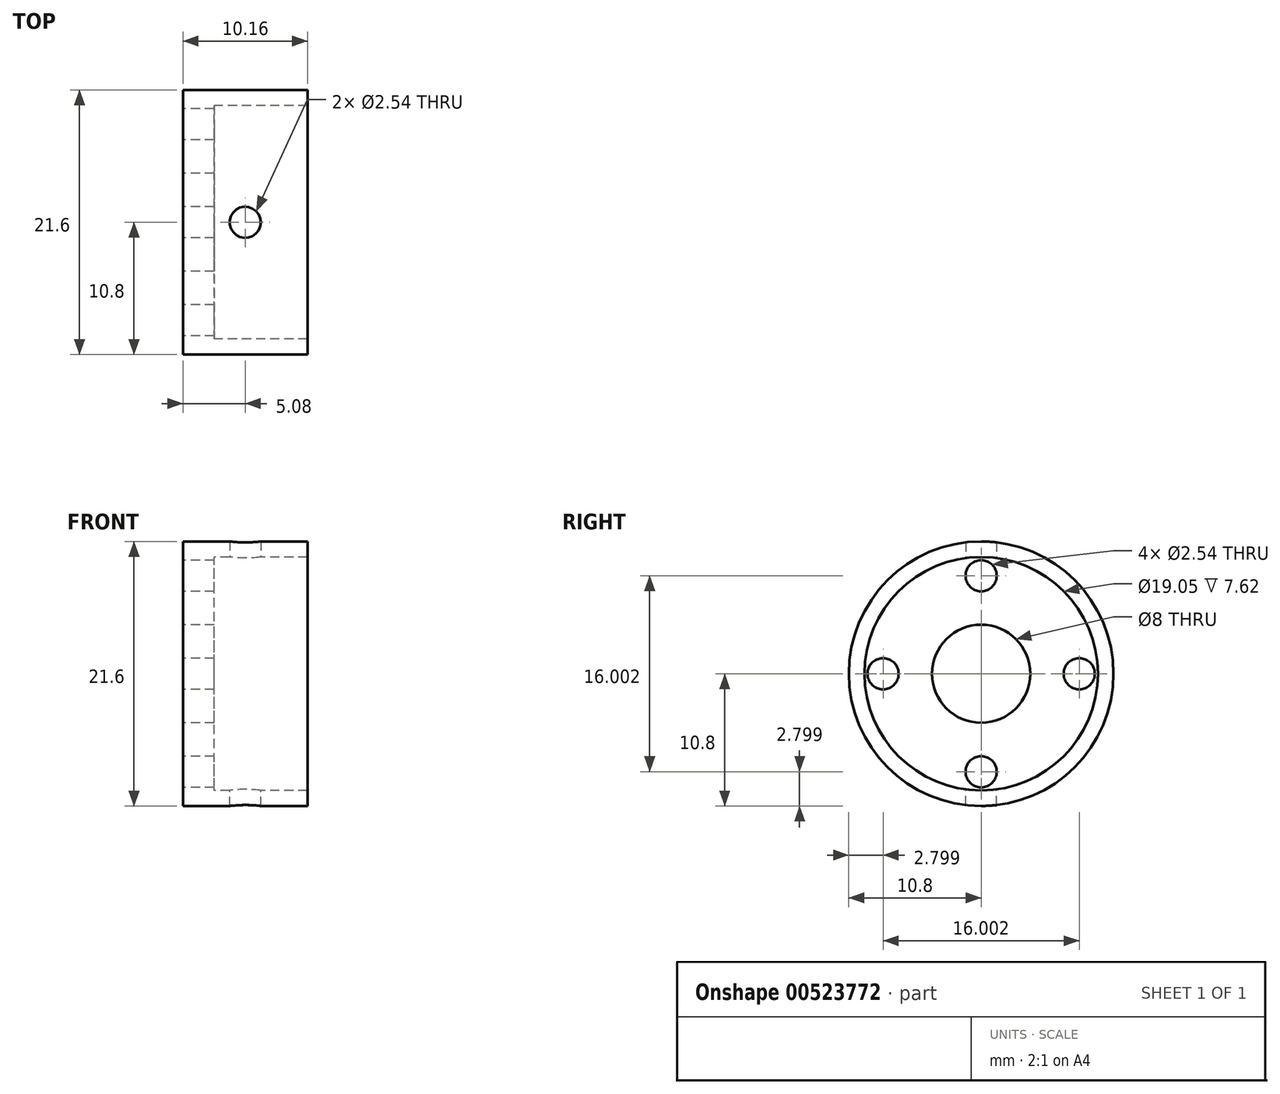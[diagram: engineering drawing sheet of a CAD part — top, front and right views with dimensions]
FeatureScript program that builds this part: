
annotation { "Feature Type Name" : "Feature", "Feature Type Description" : "" }
export const myFeature = defineFeature(function(context is Context, id is Id, definition is map)
    precondition{}
    {
        {
            var Q0;
            Q0=qCreatedBy(makeId("Right.planeOp"),FACE);
            var sketch = newSketch(context, id + "F0", { "sketchPlane" : qUnion([Q0])});
            skCircle(sketch, "E0", {"center": v(0, 0) * mm, "radius": 10.8 * mm});
            skCircle(sketch, "E1", {"center": v(0, 0) * mm, "radius": 9.53 * mm});
            skSolve(sketch);
        }
        {
            var Q0;
            Q0=makeQuery(id+"F0.imprint","IMPRINT",FACE,{"disambiguationData":[TD([[makeQuery(id+"F0.imprint","IMPRINT",EDGE,{"derivedFrom":sQuery(id+"F0.wireOp",EDGE,"E0")}),1.0]])]});
            extrude(context, id + "F1", {"entities" : qUnion([Q0]), "depth" : 10.16 * mm, "offsetDistance" : 25.4 * mm});
        }
        {
            var Q0;
            Q0=makeQuery(id+"F0.imprint","IMPRINT",FACE,{"disambiguationData":[TD([[makeQuery(id+"F0.imprint","IMPRINT",EDGE,{"derivedFrom":sQuery(id+"F0.wireOp",EDGE,"E1")}),1.0]])]});
            extrude(context, id + "F2", {"entities" : qUnion([Q0]), "operationType" : NewBodyOperationType.ADD, "depth" : 2.54 * mm, "offsetDistance" : 25.4 * mm});
        }
        {
            var Q0;
            Q0=qCreatedBy(makeId("Top.planeOp"),FACE);
            var sketch = newSketch(context, id + "F3", { "sketchPlane" : qUnion([Q0])});
            skLineSegment(sketch, "E2", {"start": v(0, 0) * mm, "end": v(5.08, 0) * mm});
            skCircle(sketch, "E3", {"center": v(5.08, 0) * mm, "radius": 1.27 * mm});
            skSolve(sketch);
        }
        {
            var Q0;
            Q0=makeQuery(id+"F3.imprint","IMPRINT",FACE,{"disambiguationData":[TD([[makeQuery(id+"F3.imprint","IMPRINT",EDGE,{"derivedFrom":sQuery(id+"F3.wireOp",EDGE,"E3")}),1.0]])]});
            extrude(context, id + "F4", {"entities" : qUnion([Q0]), "operationType" : NewBodyOperationType.REMOVE, "oppositeDirection" : true, "depth" : 25.4 * mm, "offsetDistance" : 25.4 * mm});
        }
        {
            var Q0;
            Q0=makeQuery(id+"F3.imprint","IMPRINT",FACE,{"disambiguationData":[TD([[makeQuery(id+"F3.imprint","IMPRINT",EDGE,{"derivedFrom":sQuery(id+"F3.wireOp",EDGE,"E3")}),1.0]])]});
            extrude(context, id + "F5", {"entities" : qUnion([Q0]), "operationType" : NewBodyOperationType.REMOVE, "depth" : 25.4 * mm, "offsetDistance" : 25.4 * mm});
        }
        {
            var Q0;
            {var subQ0=sQuery(id+"F0.wireOp",EDGE,"E1");Q0=makeQuery(id+"F2.boolean.opBoolean","MERGE",FACE,{"derivedFrom":[makeQuery(id+"F1.opExtrude","CAP_FACE",FACE,{"disambiguationData":[OSD([sQuery(id+"F0.wireOp",EDGE,"E0"),subQ0])],"isStart":true}),makeQuery(id+"F2.opExtrude","CAP_FACE",FACE,{"disambiguationData":[OSD([subQ0])],"isStart":true})]});}
            var sketch = newSketch(context, id + "F6", { "sketchPlane" : qUnion([Q0])});
            skCircle(sketch, "E4", {"center": v(0, 0) * mm, "radius": 4 * mm});
            skLineSegment(sketch, "E5", {"start": v(0, 0) * mm, "end": v(0, 8) * mm});
            skLineSegment(sketch, "E6", {"start": v(0, 0) * mm, "end": v(8, 0) * mm});
            skLineSegment(sketch, "E7", {"start": v(0, 0) * mm, "end": v(0, -8) * mm});
            skLineSegment(sketch, "E8", {"start": v(0, 0) * mm, "end": v(-8, 0) * mm});
            skCircle(sketch, "E9", {"center": v(-8, 0) * mm, "radius": 1.27 * mm});
            skCircle(sketch, "E10", {"center": v(0, 8) * mm, "radius": 1.27 * mm});
            skCircle(sketch, "E11", {"center": v(8, 0) * mm, "radius": 1.27 * mm});
            skCircle(sketch, "E12", {"center": v(0, -8) * mm, "radius": 1.27 * mm});
            skSolve(sketch);
        }
        {
            var Q0;
            Q0=makeQuery(id+"F6.imprint","IMPRINT",FACE,{"disambiguationData":[TD([[makeQuery(id+"F6.imprint","IMPRINT",EDGE,{"derivedFrom":sQuery(id+"F6.wireOp",EDGE,"E10")}),1.0]])]});
            var Q1;
            Q1=makeQuery(id+"F6.imprint","IMPRINT",FACE,{"disambiguationData":[TD([[makeQuery(id+"F6.imprint","IMPRINT",EDGE,{"derivedFrom":sQuery(id+"F6.wireOp",EDGE,"E9")}),1.0]])]});
            var Q2;
            Q2=makeQuery(id+"F6.imprint","IMPRINT",FACE,{"disambiguationData":[TD([[makeQuery(id+"F6.imprint","IMPRINT",EDGE,{"derivedFrom":sQuery(id+"F6.wireOp",EDGE,"E12")}),1.0]])]});
            var Q3;
            Q3=makeQuery(id+"F6.imprint","IMPRINT",FACE,{"disambiguationData":[TD([[makeQuery(id+"F6.imprint","IMPRINT",EDGE,{"derivedFrom":sQuery(id+"F6.wireOp",EDGE,"E11")}),1.0]])]});
            var Q4;
            {var subQ0=sQuery(id+"F6.wireOp",EDGE,"E5");var subQ1=sQuery(id+"F6.wireOp",EDGE,"E4");var subQ2=makeQuery(id+"F6.imprint","INTERSECT",VERTEX,{"derivedFrom":[subQ1,subQ0]});Q4=makeQuery(id+"F6.imprint","IMPRINT",FACE,{"disambiguationData":[TD([[makeQuery(id+"F6.imprint","IMPRINT",EDGE,{"disambiguationData":[TD([[subQ2,1.0]])],"derivedFrom":subQ1}),1.0]])]});}
            var Q5;
            {var subQ0=sQuery(id+"F6.wireOp",EDGE,"E5");var subQ1=sQuery(id+"F6.wireOp",EDGE,"E4");var subQ2=makeQuery(id+"F6.imprint","INTERSECT",VERTEX,{"derivedFrom":[subQ1,subQ0]});Q5=makeQuery(id+"F6.imprint","IMPRINT",FACE,{"disambiguationData":[TD([[makeQuery(id+"F6.imprint","IMPRINT",EDGE,{"disambiguationData":[TD([[subQ2,-1.0]])],"derivedFrom":subQ1}),1.0]])]});}
            var Q6;
            {var subQ0=sQuery(id+"F6.wireOp",EDGE,"E8");var subQ1=sQuery(id+"F6.wireOp",EDGE,"E4");var subQ2=makeQuery(id+"F6.imprint","INTERSECT",VERTEX,{"derivedFrom":[subQ1,subQ0]});Q6=makeQuery(id+"F6.imprint","IMPRINT",FACE,{"disambiguationData":[TD([[makeQuery(id+"F6.imprint","IMPRINT",EDGE,{"disambiguationData":[TD([[subQ2,-1.0]])],"derivedFrom":subQ1}),1.0]])]});}
            var Q7;
            {var subQ0=sQuery(id+"F6.wireOp",EDGE,"E6");var subQ1=sQuery(id+"F6.wireOp",EDGE,"E4");var subQ2=makeQuery(id+"F6.imprint","INTERSECT",VERTEX,{"derivedFrom":[subQ1,subQ0]});Q7=makeQuery(id+"F6.imprint","IMPRINT",FACE,{"disambiguationData":[TD([[makeQuery(id+"F6.imprint","IMPRINT",EDGE,{"disambiguationData":[TD([[subQ2,1.0]])],"derivedFrom":subQ1}),1.0]])]});}
            extrude(context, id + "F7", {"entities" : qUnion([Q0, Q1, Q2, Q3, Q4, Q5, Q6, Q7]), "operationType" : NewBodyOperationType.REMOVE, "oppositeDirection" : true, "depth" : 25.4 * mm, "offsetDistance" : 25.4 * mm});
        }
    });
